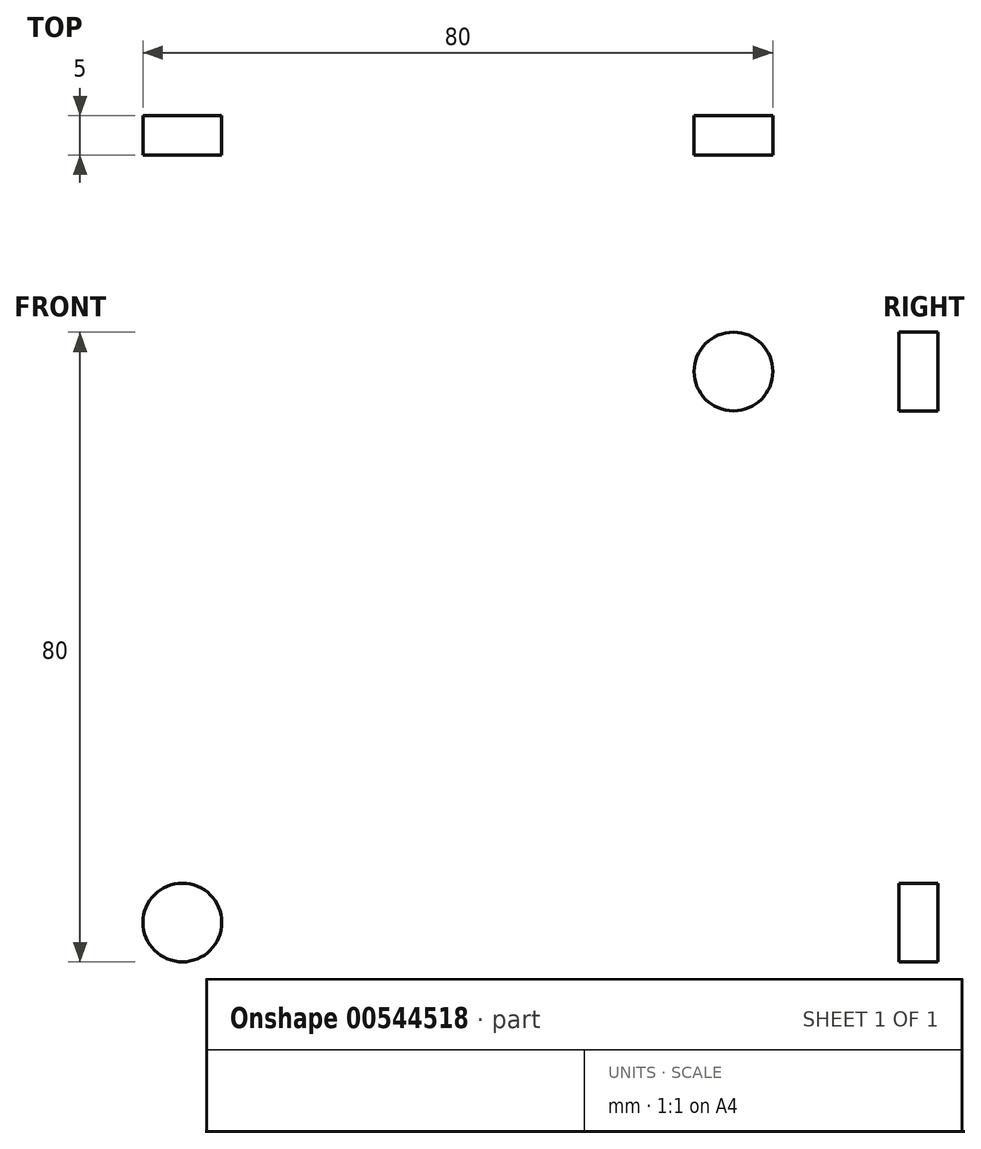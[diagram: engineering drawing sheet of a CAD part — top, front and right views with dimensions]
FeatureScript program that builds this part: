
annotation { "Feature Type Name" : "Feature", "Feature Type Description" : "" }
export const myFeature = defineFeature(function(context is Context, id is Id, definition is map)
    precondition{}
    {
        {
            var Q0;
            Q0=qCreatedBy(makeId("Front.planeOp"),FACE);
            var sketch = newSketch(context, id + "F0", { "sketchPlane" : qUnion([Q0])});
            skLineSegment(sketch, "E0.bottom", {"start": v(0, 0) * mm, "end": v(100, 0) * mm});
            skLineSegment(sketch, "E0.top", {"start": v(0, 100) * mm, "end": v(100, 100) * mm});
            skLineSegment(sketch, "E0.left", {"start": v(0, 0) * mm, "end": v(0, 100) * mm});
            skLineSegment(sketch, "E0.right", {"start": v(100, 0) * mm, "end": v(100, 100) * mm});
            skSolve(sketch);
        }
        {
            var Q0;
            Q0=makeQuery(id+"F0.imprint","IMPRINT",FACE,{"disambiguationData":[TD([[makeQuery(id+"F0.imprint","IMPRINT",EDGE,{"derivedFrom":sQuery(id+"F0.wireOp",EDGE,"E0.bottom")}),1.0]])]});
            extrude(context, id + "F1", {"entities" : qUnion([Q0]), "depth" : 5 * mm, "offsetDistance" : 25 * mm});
        }
        {
            var Q0;
            Q0=makeQuery(id+"F1.opExtrude","CAP_FACE",FACE,{"disambiguationData":[OSD([sQuery(id+"F0.wireOp",EDGE,"E0.bottom"),sQuery(id+"F0.wireOp",EDGE,"E0.top"),sQuery(id+"F0.wireOp",EDGE,"E0.left"),sQuery(id+"F0.wireOp",EDGE,"E0.right")])],"isStart":false});
            var sketch = newSketch(context, id + "F2", { "sketchPlane" : qUnion([Q0])});
            skLineSegment(sketch, "E1", {"start": v(0, 100) * mm, "end": v(15, 100) * mm, "construction": true});
            skLineSegment(sketch, "E2", {"start": v(15, 100) * mm, "end": v(15, 85) * mm, "construction": true});
            skLineSegment(sketch, "E3", {"start": v(50, 100) * mm, "end": v(50, 0) * mm, "construction": true});
            skLineSegment(sketch, "E4", {"start": v(0, 50) * mm, "end": v(100, 50) * mm, "construction": true});
            skCircle(sketch, "E5", {"center": v(15, 85) * mm, "radius": 5 * mm});
            skCircle(sketch, "E6.MirrorC", {"center": v(85, 85) * mm, "radius": 5 * mm});
            skLineSegment(sketch, "E7.MirrorCS", {"start": v(100, 50) * mm, "end": v(0, 50) * mm, "construction": true});
            skCircle(sketch, "E8.MirrorC", {"center": v(85, 15) * mm, "radius": 5 * mm});
            skCircle(sketch, "E9.MirrorC", {"center": v(15, 15) * mm, "radius": 5 * mm});
            skSolve(sketch);
        }
        {
            var Q0;
            Q0=makeQuery(id+"F2.imprint","IMPRINT",FACE,{"disambiguationData":[TD([[makeQuery(id+"F2.imprint","IMPRINT",EDGE,{"derivedFrom":sQuery(id+"F2.wireOp",EDGE,"E5")}),1.0]])]});
            var Q1;
            Q1=makeQuery(id+"F2.imprint","IMPRINT",FACE,{"disambiguationData":[TD([[makeQuery(id+"F2.imprint","IMPRINT",EDGE,{"derivedFrom":sQuery(id+"F2.wireOp",EDGE,"E6.MirrorC")}),-1.0]])]});
            var Q2;
            Q2=makeQuery(id+"F2.imprint","IMPRINT",FACE,{"disambiguationData":[TD([[makeQuery(id+"F2.imprint","IMPRINT",EDGE,{"derivedFrom":sQuery(id+"F2.wireOp",EDGE,"E9.MirrorC")}),-1.0]])]});
            var Q3;
            Q3=makeQuery(id+"F2.imprint","IMPRINT",FACE,{"disambiguationData":[TD([[makeQuery(id+"F2.imprint","IMPRINT",EDGE,{"derivedFrom":sQuery(id+"F2.wireOp",EDGE,"E8.MirrorC")}),1.0]])]});
            extrude(context, id + "F3", {"entities" : qUnion([Q0, Q1, Q2, Q3]), "operationType" : NewBodyOperationType.REMOVE, "endBound" : BoundingType.THROUGH_ALL, "oppositeDirection" : true, "depth" : 25 * mm, "offsetDistance" : 25 * mm});
        }
    });
